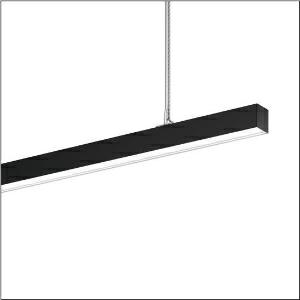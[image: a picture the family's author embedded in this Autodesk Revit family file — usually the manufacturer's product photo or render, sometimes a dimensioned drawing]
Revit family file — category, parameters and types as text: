
# Revit family: silica_r__21_51mx33db49bb_8fe2
name_source: partatom
category: Lighting Fixtures
units: mm (PartAtom-declared; Revit-internal decimal feet)

## family parameters
Cut with Voids When Loaded = No
Host = Face
Light Source = No
Part Type = Normal
Room Calculation Point = No
Round Connector Dimension = Use Diameter
Shared = No

## types (1)
- --- (1 x LED, 7390 lm, 48.3 W, 4000K)
    Apparent Load = 48 VA
    CIE Flux Codes = 78 96 99 55 100
    Color Rendering = 80
    Color Temperature = 4000K
    Default Elevation = 1800 mm
    Description = Silica® 21, office luminaire, primary optical cover: prismatic diffuser, of PMMA, CAT 2 (L<= 3000cd/m²), light emission: direct/indirect distribution, primary light characteristic: symmetric, installation type: suspended mounting, LED, rated luminous flux: 7.390lm, luminous efficacy: 153lm/W, light colour: 840, colour temperature: 4000K, with terminal, 3+2-pole, max. 2.5mm², mains connection: 220..240V, AC, 50/60Hz, rated input power: 48.3W, luminaire housing, of aluminium, jet black (RAL 9005), length: 1.504mm, width: 53mm, height: 53mm, protection rating (complete): IP20, insulation class (complete): insulation class I (protective earthing), certification: CE, permissible operating ambient temperature: 0..+35°C, standard: EN 50419, packaging unit: 1 piece
    Height = 53 mm
    Lamp = 1 x LED
    Lamp Light Flux = 7390 lm
    Lamp Power = 48.3 W
    Lamp count = 1
    Length = 1504 mm
    Luminous efficacy = 153 lm/W
    Manufacturer = Siteco
    ModVariant = No
    Model = 51MX33DB49BB
    Mounting Place = Ceiling
    Mounting Type = Pendant
    Number of Poles = 1
    OnlyDefault = Yes
    Power Factor = 1
    Product Name = Silica® 21
    Product group = office luminaire | ceiling pendant
    ProductGroupID = 902
    Protection Class = Protection class I
    Protection Degree = IP 20
    RLX_Detail_Level = 1
    RLX_Emergency_Light_Flux = 0 lm
    RLX_Emergency_Type = 0
    RLX_Emergency_Type_DB = No
    RlxData = <blob elided: 26225 chars, md5=42d8c907>
    Socket = socket
    Standby Power = 0 W
    System Light Flux = 7390 lm
    System Power = 48 W
    Type Comments = factory setting: luminous flux: 100 % | dim-lin: 254 | 323 mA
    Type Image = l_1335856.jpg
    URL = http://relux.com
    VarID = @adj_087587
    Voltage = 0 V
    Weight = 0.00 kg
    Width = 53 mm

## geometry (parser evidence)
native form markers: Blend x4, Sweep x10
no freeform markers — native parametric forms only
